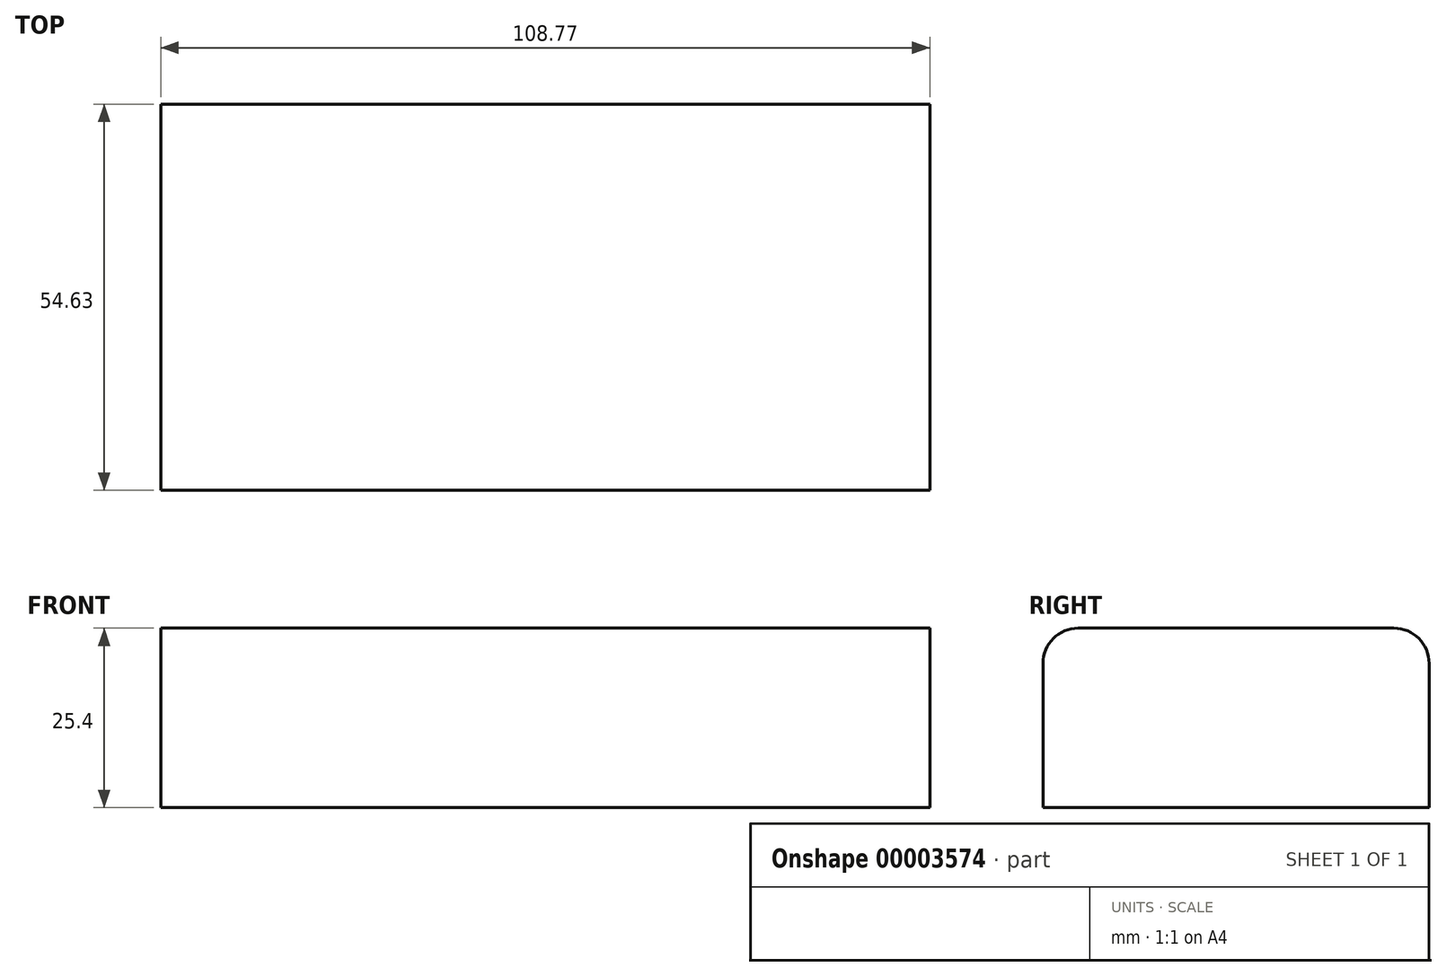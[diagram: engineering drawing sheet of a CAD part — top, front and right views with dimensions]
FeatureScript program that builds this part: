
annotation { "Feature Type Name" : "Feature", "Feature Type Description" : "" }
export const myFeature = defineFeature(function(context is Context, id is Id, definition is map)
    precondition{}
    {
        {
            var Q0;
            Q0=qCreatedBy(makeId("Top.planeOp"),FACE);
            var sketch = newSketch(context, id + "F0", { "sketchPlane" : qUnion([Q0])});
            skLineSegment(sketch, "E0.bottom", {"start": v(-66.62, 14.3) * mm, "end": v(42.15, 14.3) * mm});
            skLineSegment(sketch, "E0.top", {"start": v(-66.62, -40.32) * mm, "end": v(42.15, -40.32) * mm});
            skLineSegment(sketch, "E0.left", {"start": v(-66.62, 14.3) * mm, "end": v(-66.62, -40.32) * mm});
            skLineSegment(sketch, "E0.right", {"start": v(42.15, 14.3) * mm, "end": v(42.15, -40.32) * mm});
            skSolve(sketch);
        }
        {
            var Q0;
            Q0=makeQuery(id+"F0.imprint","IMPRINT",FACE,{"disambiguationData":[TD([[makeQuery(id+"F0.imprint","IMPRINT",EDGE,{"derivedFrom":sQuery(id+"F0.wireOp",EDGE,"E0.bottom")}),-1.0]])]});
            extrude(context, id + "F1", {"entities" : qUnion([Q0]), "endBound" : BoundingType.SYMMETRIC, "oppositeDirection" : true, "depth" : 25.4 * mm});
        }
        {
            var Q0;
            Q0=makeQuery(id+"F1.opExtrude","CAP_EDGE",EDGE,{"disambiguationData":[OSD([sQuery(id+"F0.wireOp",EDGE,"E0.top")])],"isStart":true});
            fillet(context, id + "F2", {"entities" : qUnion([Q0]), "radius" : 5 * mm, "tangentPropagation" : true, "allowEdgeOverflow" : false});
        }
        {
            var Q0;
            Q0=makeQuery(id+"F1.opExtrude","CAP_EDGE",EDGE,{"disambiguationData":[OSD([sQuery(id+"F0.wireOp",EDGE,"E0.bottom")])],"isStart":true});
            fillet(context, id + "F3", {"entities" : qUnion([Q0]), "radius" : 5 * mm, "tangentPropagation" : true, "allowEdgeOverflow" : false});
        }
    });
